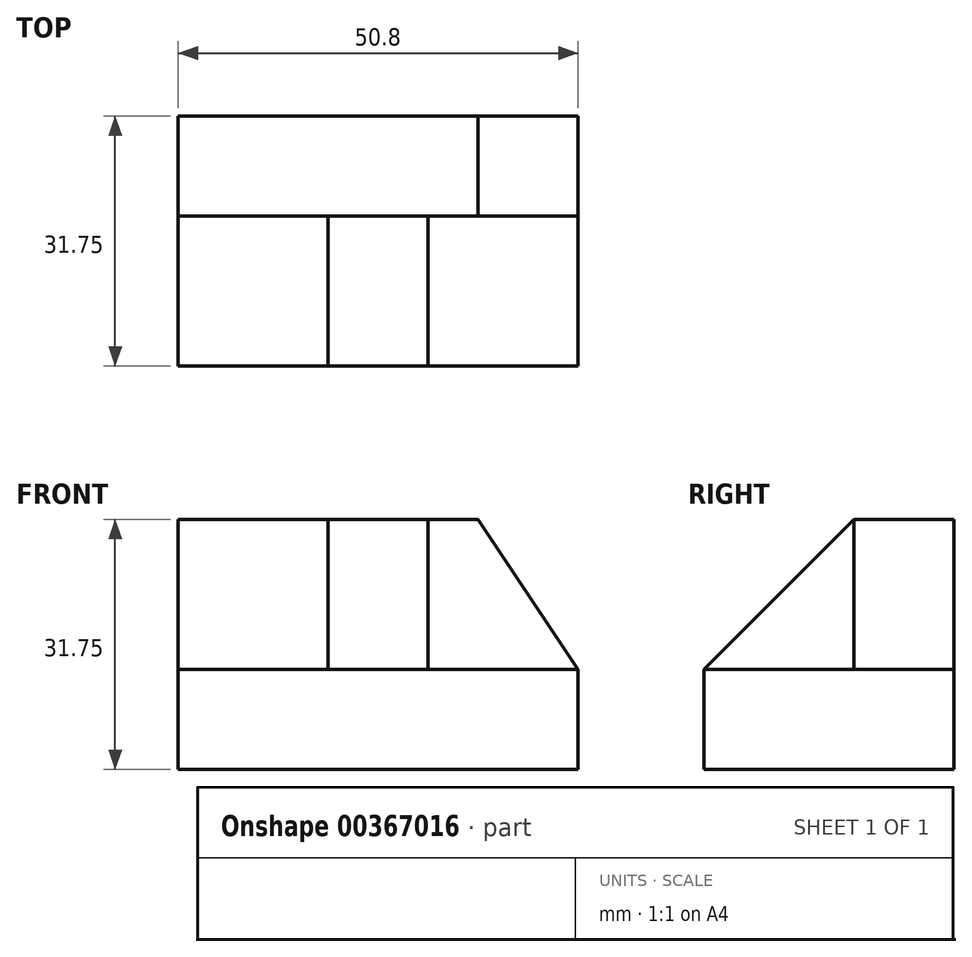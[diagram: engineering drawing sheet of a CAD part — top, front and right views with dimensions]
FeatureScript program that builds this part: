
annotation { "Feature Type Name" : "Feature", "Feature Type Description" : "" }
export const myFeature = defineFeature(function(context is Context, id is Id, definition is map)
    precondition{}
    {
        {
            var Q0;
            Q0=qCreatedBy(makeId("Right.planeOp"),FACE);
            var sketch = newSketch(context, id + "F0", { "sketchPlane" : qUnion([Q0])});
            skLineSegment(sketch, "E0.bottom", {"start": v(0, 0) * mm, "end": v(31.75, 0) * mm});
            skLineSegment(sketch, "E0.top", {"start": v(0, 31.75) * mm, "end": v(31.75, 31.75) * mm});
            skLineSegment(sketch, "E0.left", {"start": v(0, 0) * mm, "end": v(0, 31.75) * mm});
            skLineSegment(sketch, "E0.right", {"start": v(31.75, 0) * mm, "end": v(31.75, 31.75) * mm});
            skSolve(sketch);
        }
        {
            var Q0;
            Q0 = qSketchRegion(id + "F0", true);
            extrude(context, id + "F1", {"entities" : qUnion([Q0]), "depth" : 50.8 * mm});
        }
        {
            var Q0;
            Q0=makeQuery(id+"F1.opExtrude","CAP_FACE",FACE,{"disambiguationData":[OSD([sQuery(id+"F0.wireOp",EDGE,"E0.bottom"),sQuery(id+"F0.wireOp",EDGE,"E0.top"),sQuery(id+"F0.wireOp",EDGE,"E0.left"),sQuery(id+"F0.wireOp",EDGE,"E0.right")])],"isStart":false});
            var sketch = newSketch(context, id + "F2", { "sketchPlane" : qUnion([Q0])});
            skLineSegment(sketch, "E1.bottom", {"start": v(19.05, 12.7) * mm, "end": v(0, 12.7) * mm});
            skLineSegment(sketch, "E1.top", {"start": v(19.05, 31.75) * mm, "end": v(0, 31.75) * mm});
            skLineSegment(sketch, "E1.left", {"start": v(19.05, 12.7) * mm, "end": v(19.05, 31.75) * mm});
            skLineSegment(sketch, "E1.right", {"start": v(0, 12.7) * mm, "end": v(0, 31.75) * mm});
            skSolve(sketch);
        }
        {
            var Q0;
            Q0 = qSketchRegion(id + "F2", true);
            extrude(context, id + "F3", {"entities" : qUnion([Q0]), "operationType" : NewBodyOperationType.REMOVE, "oppositeDirection" : true, "depth" : 19.05 * mm});
        }
        {
            var Q0;
            Q0=makeQuery(id+"F1.opExtrude","CAP_FACE",FACE,{"disambiguationData":[OSD([sQuery(id+"F0.wireOp",EDGE,"E0.bottom"),sQuery(id+"F0.wireOp",EDGE,"E0.top"),sQuery(id+"F0.wireOp",EDGE,"E0.left"),sQuery(id+"F0.wireOp",EDGE,"E0.right")])],"isStart":true});
            var sketch = newSketch(context, id + "F4", { "sketchPlane" : qUnion([Q0])});
            skLineSegment(sketch, "E2.bottom", {"start": v(-19.05, 31.75) * mm, "end": v(0, 31.75) * mm});
            skLineSegment(sketch, "E2.top", {"start": v(-19.05, 12.7) * mm, "end": v(0, 12.7) * mm});
            skLineSegment(sketch, "E2.left", {"start": v(-19.05, 31.75) * mm, "end": v(-19.05, 12.7) * mm});
            skLineSegment(sketch, "E2.right", {"start": v(0, 31.75) * mm, "end": v(0, 12.7) * mm});
            skSolve(sketch);
        }
        {
            var Q0;
            Q0 = qSketchRegion(id + "F4", true);
            extrude(context, id + "F5", {"entities" : qUnion([Q0]), "operationType" : NewBodyOperationType.REMOVE, "oppositeDirection" : true, "depth" : 19.05 * mm});
        }
        {
            var Q0;
            Q0=makeQuery(id+"F5.boolean.opBoolean","COPY",FACE,{"derivedFrom":makeQuery(id+"F5.opExtrude","CAP_FACE",FACE,{"disambiguationData":[OSD([sQuery(id+"F4.wireOp",EDGE,"E2.bottom"),sQuery(id+"F4.wireOp",EDGE,"E2.top"),sQuery(id+"F4.wireOp",EDGE,"E2.left"),sQuery(id+"F4.wireOp",EDGE,"E2.right")])],"isStart":false})});
            var sketch = newSketch(context, id + "F6", { "sketchPlane" : qUnion([Q0])});
            skLineSegment(sketch, "E3", {"start": v(-19.05, 31.75) * mm, "end": v(0, 12.7) * mm});
            skLineSegment(sketch, "E4", {"start": v(-19.05, 31.75) * mm, "end": v(0, 31.75) * mm});
            skLineSegment(sketch, "E5", {"start": v(0, 31.75) * mm, "end": v(0, 12.7) * mm});
            skSolve(sketch);
        }
        {
            var Q0;
            Q0 = qSketchRegion(id + "F6", true);
            extrude(context, id + "F7", {"entities" : qUnion([Q0]), "operationType" : NewBodyOperationType.REMOVE, "oppositeDirection" : true, "depth" : 25.4 * mm});
        }
        {
            var Q0;
            Q0=makeQuery(id+"F3.boolean.opBoolean","COPY",FACE,{"derivedFrom":makeQuery(id+"F3.opExtrude","SWEPT_FACE",FACE,{"disambiguationData":[OSD([sQuery(id+"F2.wireOp",EDGE,"E1.left")])]})});
            var sketch = newSketch(context, id + "F8", { "sketchPlane" : qUnion([Q0])});
            skLineSegment(sketch, "E6", {"start": v(50.8, 12.7) * mm, "end": v(38.1, 31.75) * mm});
            skLineSegment(sketch, "E7", {"start": v(38.1, 31.75) * mm, "end": v(50.8, 31.75) * mm});
            skLineSegment(sketch, "E8", {"start": v(50.8, 31.75) * mm, "end": v(50.8, 12.7) * mm});
            skSolve(sketch);
        }
        {
            var Q0;
            Q0 = qSketchRegion(id + "F8", true);
            extrude(context, id + "F9", {"entities" : qUnion([Q0]), "operationType" : NewBodyOperationType.REMOVE, "oppositeDirection" : true, "depth" : 25.4 * mm});
        }
    });
